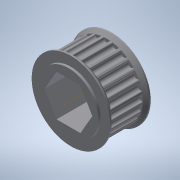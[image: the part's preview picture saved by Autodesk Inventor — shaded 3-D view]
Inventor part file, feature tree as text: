
AUTODESK INVENTOR PART (.ipt)
format: ipt  version: 2022.3 (Build 263350000, 350)  size: 340,480 bytes
history: native  units: in
note: dims shown in document units (in); Inventor stores cm internally (conversion verified against a paired STEP export)
features: sketch x8, extrude x7, mirror x2, chamfer x2, other x1, fillet x1, pattern_circular x1
ambient origin geometry x8: Origin, YZ Plane, XZ Plane, XY Plane, X Axis, Y Axis, Z Axis, Center Point
bodies: Solid1 (feature_tree)
feature tree (22):
  other  "Hex Bore"
  extrude  "HTD Base"  Depth=0.3937in TaperAngle=0.0deg
  extrude  "HTD Flange"  Depth=0.0591in
  mirror  "HTD Flanges"
  chamfer  "HTD Flange Chamfer"  Distance=0.0787in Angle=45.0deg
  extrude  "GT2 Base"  TaperAngle=0.0deg  [1 undecoded]
  extrude  "GT2 Base Tooth"  TaperAngle=0.0deg  [1 undecoded]
  fillet  "GT2 Base Tooth pt. 2"  Radius=0.9099in
  pattern_circular  "GT2 Teeth"  [2 undecoded]
  extrude  "GT2 Flange"  Depth=0.03in
  mirror  "GT2 Flanges"
  chamfer  "GT2 Flange Chamfer"  [1 undecoded]
  extrude  "Circle Bore"  Depth=0.0118in
  extrude  "Extrusion9"  Depth=0.03in
  sketch  "Sketch1"  dims[d0=1.5215in d1=0.3937in d2=0.0in]
  sketch  "Sketch3"  dims[d12=0.0394in d13=0.0591in]
  sketch  "Sketch4"  dims[d14=0.0in]
  sketch  "Sketch5"  dims[d15=0.0394in d16=0.0787in d17=45.0deg]
  sketch  "Sketch6"  dims[d18=0.52in d19=0.0in d20=0.0in]
  sketch  "Sketch7"  dims[d21=0.52in d22=0.0in d23=0.0in d24=0.9099in]
  sketch  "Sketch8"  dims[d25=0.3937in]
  sketch  "Sketch9"  dims[d26=0.0in d27=0.0727in d28=0.0075in d29=0.0in d30=0.0in d31=0.0118in d32=9.8425in d33=360.0deg d35=0.0394in d36=0.0591in d37=0.0in d38=0.0394in d39=0.0787in d40=45.0deg d41=0.75in d42=0.03in d43=0.0in]
note: 5 required parameter values undecoded (feature->parameter linkage not recoverable at this tier; creation-order binding heuristic only, values carry confidence <= 0.55)
